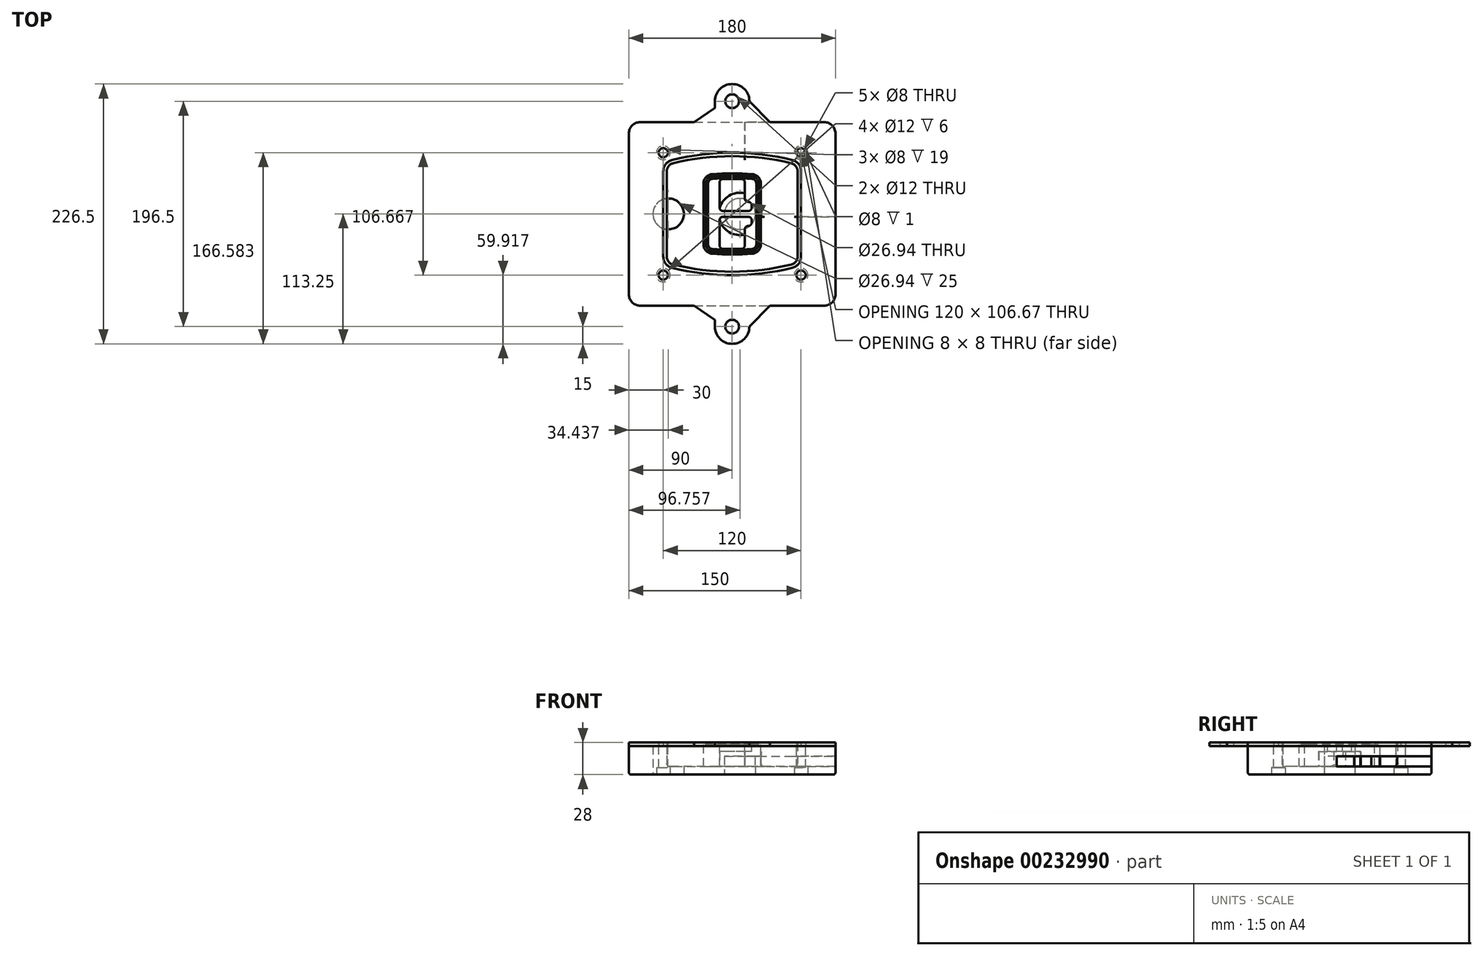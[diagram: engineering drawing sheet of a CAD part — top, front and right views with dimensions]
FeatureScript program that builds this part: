
annotation { "Feature Type Name" : "Feature", "Feature Type Description" : "" }
export const myFeature = defineFeature(function(context is Context, id is Id, definition is map)
    precondition{}
    {
        {
            var Q0;
            Q0=qCreatedBy(makeId("Top.planeOp"),FACE);
            var sketch = newSketch(context, id + "F0", { "sketchPlane" : qUnion([Q0])});
            skPoint(sketch, "E0.rect.middle", {"position": v(0, 0) * mm});
            skLineSegment(sketch, "E1.bottom", {"start": v(-80, -80) * mm, "end": v(80, -80) * mm});
            skLineSegment(sketch, "E1.top", {"start": v(-80, 80) * mm, "end": v(80, 80) * mm});
            skLineSegment(sketch, "E1.left", {"start": v(-90, -70) * mm, "end": v(-90, 70) * mm});
            skLineSegment(sketch, "E1.right", {"start": v(90, -70) * mm, "end": v(90, 70) * mm});
            skLineSegment(sketch, "E2", {"start": v(-90, 80) * mm, "end": v(90, -80) * mm, "construction": true});
            skLineSegment(sketch, "E3", {"start": v(90, 80) * mm, "end": v(-90, -80) * mm, "construction": true});
            skCircle(sketch, "E4", {"center": v(-60, 53.33) * mm, "radius": 4 * mm});
            skCircle(sketch, "E5", {"center": v(60, 53.33) * mm, "radius": 4 * mm});
            skCircle(sketch, "E6", {"center": v(60, -53.33) * mm, "radius": 4 * mm});
            skCircle(sketch, "E7", {"center": v(-60, -53.33) * mm, "radius": 4 * mm});
            skLineSegment(sketch, "E8", {"start": v(-60, 53.33) * mm, "end": v(60, 53.33) * mm, "construction": true});
            skLineSegment(sketch, "E9", {"start": v(60, 53.33) * mm, "end": v(60, -53.33) * mm, "construction": true});
            skLineSegment(sketch, "E10", {"start": v(60, -53.33) * mm, "end": v(-60, -53.33) * mm, "construction": true});
            skLineSegment(sketch, "E11", {"start": v(-60, -53.33) * mm, "end": v(-60, 53.33) * mm, "construction": true});
            skLineSegment(sketch, "E12", {"start": v(-60, 37.3) * mm, "end": v(-60, -37.3) * mm});
            skLineSegment(sketch, "E13", {"start": v(60, 37.3) * mm, "end": v(60, -37.3) * mm});
            skArc(sketch, "E14", {"start": v(52.38, 47.01) * mm, "mid": v(0, 53.33) * mm, "end": v(-52.38, 47.01) * mm});
            skArc(sketch, "E15", {"start": v(-52.38, -47.01) * mm, "mid": v(0, -53.33) * mm, "end": v(52.38, -47.01) * mm});
            skLineSegment(sketch, "E16", {"start": v(-60, 0) * mm, "end": v(60, 0) * mm, "construction": true});
            skPoint(sketch, "E17.visualSharp", {"position": v(-60, -45) * mm});
            skArc(sketch, "E17.filletArc", {"start": v(-60, -37.3) * mm, "mid": v(-57.87, -43.47) * mm, "end": v(-52.38, -47.01) * mm});
            skPoint(sketch, "E18.visualSharp", {"position": v(-60, 45) * mm});
            skArc(sketch, "E18.filletArc", {"start": v(-52.38, 47.01) * mm, "mid": v(-57.87, 43.47) * mm, "end": v(-60, 37.3) * mm});
            skPoint(sketch, "E19.visualSharp", {"position": v(60, 45) * mm});
            skArc(sketch, "E19.filletArc", {"start": v(60, 37.3) * mm, "mid": v(57.87, 43.47) * mm, "end": v(52.38, 47.01) * mm});
            skPoint(sketch, "E20.visualSharp", {"position": v(60, -45) * mm});
            skArc(sketch, "E20.filletArc", {"start": v(52.38, -47.01) * mm, "mid": v(57.87, -43.47) * mm, "end": v(60, -37.3) * mm});
            skPoint(sketch, "E21.visualSharp", {"position": v(-90, 80) * mm});
            skArc(sketch, "E21.filletArc", {"start": v(-80, 80) * mm, "mid": v(-87.07, 77.07) * mm, "end": v(-90, 70) * mm});
            skPoint(sketch, "E22.visualSharp", {"position": v(90, 80) * mm});
            skArc(sketch, "E22.filletArc", {"start": v(90, 70) * mm, "mid": v(87.07, 77.07) * mm, "end": v(80, 80) * mm});
            skPoint(sketch, "E23.visualSharp", {"position": v(90, -80) * mm});
            skArc(sketch, "E23.filletArc", {"start": v(80, -80) * mm, "mid": v(87.07, -77.07) * mm, "end": v(90, -70) * mm});
            skPoint(sketch, "E24.visualSharp", {"position": v(-90, -80) * mm});
            skArc(sketch, "E24.filletArc", {"start": v(-90, -70) * mm, "mid": v(-87.07, -77.07) * mm, "end": v(-80, -80) * mm});
            skArc(sketch, "E25.0", {"start": v(57, 37.3) * mm, "mid": v(55.5, 41.62) * mm, "end": v(51.67, 44.1) * mm});
            skLineSegment(sketch, "E25.1", {"start": v(57, 37.3) * mm, "end": v(57, -37.3) * mm});
            skArc(sketch, "E25.2", {"start": v(51.67, -44.1) * mm, "mid": v(55.5, -41.62) * mm, "end": v(57, -37.3) * mm});
            skArc(sketch, "E25.3", {"start": v(-51.67, -44.1) * mm, "mid": v(0, -50.33) * mm, "end": v(51.67, -44.1) * mm});
            skArc(sketch, "E25.4", {"start": v(-57, -37.3) * mm, "mid": v(-55.5, -41.62) * mm, "end": v(-51.67, -44.1) * mm});
            skArc(sketch, "E25.5", {"start": v(51.67, 44.1) * mm, "mid": v(0, 50.33) * mm, "end": v(-51.67, 44.1) * mm});
            skLineSegment(sketch, "E25.6", {"start": v(-57, 37.3) * mm, "end": v(-57, -37.3) * mm});
            skArc(sketch, "E25.7", {"start": v(-51.67, 44.1) * mm, "mid": v(-55.5, 41.62) * mm, "end": v(-57, 37.3) * mm});
            skArc(sketch, "E26.0", {"start": v(-53.33, 50.9) * mm, "mid": v(-61.01, 45.94) * mm, "end": v(-64, 37.3) * mm});
            skArc(sketch, "E26.1", {"start": v(53.33, 50.9) * mm, "mid": v(0, 57.33) * mm, "end": v(-53.33, 50.9) * mm});
            skArc(sketch, "E26.2", {"start": v(64, 37.3) * mm, "mid": v(61.01, 45.94) * mm, "end": v(53.33, 50.9) * mm});
            skLineSegment(sketch, "E26.3", {"start": v(64, 37.3) * mm, "end": v(64, -37.3) * mm});
            skArc(sketch, "E26.4", {"start": v(53.33, -50.9) * mm, "mid": v(61.01, -45.94) * mm, "end": v(64, -37.3) * mm});
            skLineSegment(sketch, "E26.5", {"start": v(-64, 37.3) * mm, "end": v(-64, -37.3) * mm});
            skArc(sketch, "E26.6", {"start": v(-53.33, -50.9) * mm, "mid": v(0, -57.33) * mm, "end": v(53.33, -50.9) * mm});
            skArc(sketch, "E26.7", {"start": v(-64, -37.3) * mm, "mid": v(-61.01, -45.94) * mm, "end": v(-53.33, -50.9) * mm});
            skSolve(sketch);
        }
        {
            var Q0;
            Q0=makeQuery(id+"F0.imprint","IMPRINT",FACE,{"disambiguationData":[TD([[makeQuery(id+"F0.imprint","IMPRINT",EDGE,{"derivedFrom":sQuery(id+"F0.wireOp",EDGE,"E1.bottom")}),1.0]])]});
            var Q1;
            Q1=makeQuery(id+"F0.imprint","IMPRINT",FACE,{"disambiguationData":[TD([[makeQuery(id+"F0.imprint","IMPRINT",EDGE,{"derivedFrom":sQuery(id+"F0.wireOp",EDGE,"E12")}),1.0]])]});
            var Q2;
            Q2=makeQuery(id+"F0.imprint","IMPRINT",FACE,{"disambiguationData":[TD([[makeQuery(id+"F0.imprint","IMPRINT",EDGE,{"derivedFrom":sQuery(id+"F0.wireOp",EDGE,"E25.0")}),1.0]])]});
            var Q3;
            Q3=makeQuery(id+"F0.imprint","IMPRINT",FACE,{"disambiguationData":[TD([[makeQuery(id+"F0.imprint","IMPRINT",EDGE,{"derivedFrom":sQuery(id+"F0.wireOp",EDGE,"E12")}),-1.0]])]});
            extrude(context, id + "F1", {"entities" : qUnion([Q0, Q1, Q2, Q3]), "oppositeDirection" : true, "depth" : 25 * mm});
        }
        {
            var Q0;
            Q0=makeQuery(id+"F0.imprint","IMPRINT",FACE,{"disambiguationData":[TD([[makeQuery(id+"F0.imprint","IMPRINT",EDGE,{"derivedFrom":sQuery(id+"F0.wireOp",EDGE,"E12")}),1.0]])]});
            extrude(context, id + "F2", {"entities" : qUnion([Q0]), "operationType" : NewBodyOperationType.ADD, "depth" : 3 * mm});
        }
        {
            var Q0;
            Q0=makeQuery(id+"F0.imprint","IMPRINT",FACE,{"disambiguationData":[TD([[makeQuery(id+"F0.imprint","IMPRINT",EDGE,{"derivedFrom":sQuery(id+"F0.wireOp",EDGE,"E25.0")}),1.0]])]});
            extrude(context, id + "F3", {"entities" : qUnion([Q0]), "operationType" : NewBodyOperationType.REMOVE, "oppositeDirection" : true, "depth" : 18 * mm});
        }
        {
            var Q0;
            Q0=makeQuery(id+"F2.opExtrude","CAP_FACE",FACE,{"disambiguationData":[OSD([sQuery(id+"F0.wireOp",EDGE,"E12"),sQuery(id+"F0.wireOp",EDGE,"E13"),sQuery(id+"F0.wireOp",EDGE,"E14"),sQuery(id+"F0.wireOp",EDGE,"E15"),sQuery(id+"F0.wireOp",EDGE,"E17.filletArc"),sQuery(id+"F0.wireOp",EDGE,"E18.filletArc"),sQuery(id+"F0.wireOp",EDGE,"E19.filletArc"),sQuery(id+"F0.wireOp",EDGE,"E20.filletArc"),sQuery(id+"F0.wireOp",EDGE,"E25.0"),sQuery(id+"F0.wireOp",EDGE,"E25.1"),sQuery(id+"F0.wireOp",EDGE,"E25.2"),sQuery(id+"F0.wireOp",EDGE,"E25.3"),sQuery(id+"F0.wireOp",EDGE,"E25.4"),sQuery(id+"F0.wireOp",EDGE,"E25.5"),sQuery(id+"F0.wireOp",EDGE,"E25.6"),sQuery(id+"F0.wireOp",EDGE,"E25.7")])],"isStart":false});
            var sketch = newSketch(context, id + "F4", { "sketchPlane" : qUnion([Q0])});
            skArc(sketch, "E27.0", {"start": v(-17.7, -34.56) * mm, "mid": v(0, -35.33) * mm, "end": v(17.7, -34.56) * mm});
            skArc(sketch, "E28.0", {"start": v(17.7, 34.56) * mm, "mid": v(0, 35.33) * mm, "end": v(-17.7, 34.56) * mm});
            skLineSegment(sketch, "E29", {"start": v(-25, 26.59) * mm, "end": v(-25, -26.59) * mm});
            skLineSegment(sketch, "E30", {"start": v(25, 26.59) * mm, "end": v(25, -26.59) * mm});
            skLineSegment(sketch, "E31", {"start": v(-25, 33.78) * mm, "end": v(25, 33.78) * mm, "construction": true});
            skLineSegment(sketch, "E32", {"start": v(-25, -33.78) * mm, "end": v(25, -33.78) * mm, "construction": true});
            skPoint(sketch, "E33.visualSharp", {"position": v(-25, 33.78) * mm});
            skArc(sketch, "E33.filletArc", {"start": v(-17.7, 34.56) * mm, "mid": v(-22.9, 32) * mm, "end": v(-25, 26.59) * mm});
            skPoint(sketch, "E34.visualSharp", {"position": v(25, 33.78) * mm});
            skArc(sketch, "E34.filletArc", {"start": v(25, 26.59) * mm, "mid": v(22.9, 32) * mm, "end": v(17.7, 34.56) * mm});
            skPoint(sketch, "E35.visualSharp", {"position": v(25, -33.78) * mm});
            skArc(sketch, "E35.filletArc", {"start": v(17.7, -34.56) * mm, "mid": v(22.9, -32) * mm, "end": v(25, -26.59) * mm});
            skPoint(sketch, "E36.visualSharp", {"position": v(-25, -33.78) * mm});
            skArc(sketch, "E36.filletArc", {"start": v(-25, -26.59) * mm, "mid": v(-22.9, -32) * mm, "end": v(-17.7, -34.56) * mm});
            skArc(sketch, "E37.0", {"start": v(51.67, 44.1) * mm, "mid": v(0, 50.33) * mm, "end": v(-51.67, 44.1) * mm});
            skArc(sketch, "E37.1", {"start": v(-51.67, 44.1) * mm, "mid": v(-55.5, 41.62) * mm, "end": v(-57, 37.3) * mm});
            skLineSegment(sketch, "E37.2", {"start": v(-57, 37.3) * mm, "end": v(-57, -37.3) * mm});
            skArc(sketch, "E37.3", {"start": v(-57, -37.3) * mm, "mid": v(-55.5, -41.62) * mm, "end": v(-51.67, -44.1) * mm});
            skArc(sketch, "E37.4", {"start": v(-51.67, -44.1) * mm, "mid": v(0, -50.33) * mm, "end": v(51.67, -44.1) * mm});
            skArc(sketch, "E37.5", {"start": v(51.67, -44.1) * mm, "mid": v(55.5, -41.62) * mm, "end": v(57, -37.3) * mm});
            skLineSegment(sketch, "E37.6", {"start": v(57, 37.3) * mm, "end": v(57, -37.3) * mm});
            skArc(sketch, "E37.7", {"start": v(57, 37.3) * mm, "mid": v(55.5, 41.62) * mm, "end": v(51.67, 44.1) * mm});
            skLineSegment(sketch, "E38.0", {"start": v(23, 26.59) * mm, "end": v(23, -26.59) * mm});
            skArc(sketch, "E38.1", {"start": v(17.53, -32.56) * mm, "mid": v(21.42, -30.64) * mm, "end": v(23, -26.59) * mm});
            skArc(sketch, "E38.2", {"start": v(-17.53, -32.56) * mm, "mid": v(0, -33.33) * mm, "end": v(17.53, -32.56) * mm});
            skArc(sketch, "E38.3", {"start": v(-23, -26.59) * mm, "mid": v(-21.42, -30.64) * mm, "end": v(-17.53, -32.56) * mm});
            skLineSegment(sketch, "E38.4", {"start": v(-23, 26.59) * mm, "end": v(-23, -26.59) * mm});
            skArc(sketch, "E38.5", {"start": v(23, 26.59) * mm, "mid": v(21.42, 30.64) * mm, "end": v(17.53, 32.56) * mm});
            skArc(sketch, "E38.6", {"start": v(-17.53, 32.56) * mm, "mid": v(-21.42, 30.64) * mm, "end": v(-23, 26.59) * mm});
            skArc(sketch, "E38.7", {"start": v(17.53, 32.56) * mm, "mid": v(0, 33.33) * mm, "end": v(-17.53, 32.56) * mm});
            skArc(sketch, "E39.0", {"start": v(21, 26.59) * mm, "mid": v(19.95, 29.29) * mm, "end": v(17.35, 30.57) * mm});
            skLineSegment(sketch, "E39.1", {"start": v(21, 26.59) * mm, "end": v(21, -26.59) * mm});
            skArc(sketch, "E39.2", {"start": v(17.35, -30.57) * mm, "mid": v(19.95, -29.29) * mm, "end": v(21, -26.59) * mm});
            skArc(sketch, "E39.3", {"start": v(-17.35, -30.57) * mm, "mid": v(0, -31.33) * mm, "end": v(17.35, -30.57) * mm});
            skArc(sketch, "E39.4", {"start": v(-21, -26.59) * mm, "mid": v(-19.95, -29.29) * mm, "end": v(-17.35, -30.57) * mm});
            skArc(sketch, "E39.5", {"start": v(17.35, 30.57) * mm, "mid": v(0, 31.33) * mm, "end": v(-17.35, 30.57) * mm});
            skLineSegment(sketch, "E39.6", {"start": v(-21, 26.59) * mm, "end": v(-21, -26.59) * mm});
            skArc(sketch, "E39.7", {"start": v(-17.35, 30.57) * mm, "mid": v(-19.95, 29.29) * mm, "end": v(-21, 26.59) * mm});
            skLineSegment(sketch, "E40", {"start": v(-25, 0) * mm, "end": v(25, 0) * mm, "construction": true});
            skLineSegment(sketch, "E41", {"start": v(-11, 5.5) * mm, "end": v(-11, 27.5) * mm});
            skLineSegment(sketch, "E42", {"start": v(-8, 30.5) * mm, "end": v(8, 30.5) * mm});
            skLineSegment(sketch, "E43", {"start": v(11, 27.5) * mm, "end": v(11, 13.5) * mm});
            skLineSegment(sketch, "E44", {"start": v(14, 10.5) * mm, "end": v(14, 10.5) * mm});
            skLineSegment(sketch, "E45", {"start": v(17, 7.5) * mm, "end": v(17, 5.5) * mm});
            skLineSegment(sketch, "E46", {"start": v(14, 2.5) * mm, "end": v(-8, 2.5) * mm});
            skPoint(sketch, "E47.visualSharp", {"position": v(-11, 30.5) * mm});
            skArc(sketch, "E47.filletArc", {"start": v(-8, 30.5) * mm, "mid": v(-10.12, 29.62) * mm, "end": v(-11, 27.5) * mm});
            skPoint(sketch, "E48.visualSharp", {"position": v(11, 30.5) * mm});
            skArc(sketch, "E48.filletArc", {"start": v(11, 27.5) * mm, "mid": v(10.12, 29.62) * mm, "end": v(8, 30.5) * mm});
            skPoint(sketch, "E49.visualSharp", {"position": v(11, 10.5) * mm});
            skArc(sketch, "E49.filletArc", {"start": v(11, 13.5) * mm, "mid": v(11.88, 11.38) * mm, "end": v(14, 10.5) * mm});
            skPoint(sketch, "E50.visualSharp", {"position": v(17, 10.5) * mm});
            skArc(sketch, "E50.filletArc", {"start": v(17, 7.5) * mm, "mid": v(16.12, 9.62) * mm, "end": v(14, 10.5) * mm});
            skPoint(sketch, "E51.visualSharp", {"position": v(17, 2.5) * mm});
            skArc(sketch, "E51.filletArc", {"start": v(14, 2.5) * mm, "mid": v(16.12, 3.38) * mm, "end": v(17, 5.5) * mm});
            skPoint(sketch, "E52.visualSharp", {"position": v(-11, 2.5) * mm});
            skArc(sketch, "E52.filletArc", {"start": v(-11, 5.5) * mm, "mid": v(-10.12, 3.38) * mm, "end": v(-8, 2.5) * mm});
            skLineSegment(sketch, "E53.0.MirrorCS", {"start": v(14, -2.5) * mm, "end": v(-8, -2.5) * mm});
            skArc(sketch, "E54.0.MirrorCS", {"start": v(-11, -5.5) * mm, "mid": v(-10.12, -3.38) * mm, "end": v(-8, -2.5) * mm});
            skLineSegment(sketch, "E55.0.MirrorCS", {"start": v(-11, -5.5) * mm, "end": v(-11, -27.5) * mm});
            skArc(sketch, "E56.0.MirrorCS", {"start": v(-8, -30.5) * mm, "mid": v(-10.12, -29.62) * mm, "end": v(-11, -27.5) * mm});
            skLineSegment(sketch, "E57.0.MirrorCS", {"start": v(-8, -30.5) * mm, "end": v(8, -30.5) * mm});
            skArc(sketch, "E58.0.MirrorCS", {"start": v(11, -27.5) * mm, "mid": v(10.12, -29.62) * mm, "end": v(8, -30.5) * mm});
            skLineSegment(sketch, "E59.0.MirrorCS", {"start": v(11, -27.5) * mm, "end": v(11, -13.5) * mm});
            skArc(sketch, "E60.0.MirrorCS", {"start": v(11, -13.5) * mm, "mid": v(11.88, -11.38) * mm, "end": v(14, -10.5) * mm});
            skArc(sketch, "E61.0.MirrorCS", {"start": v(17, -7.5) * mm, "mid": v(16.12, -9.62) * mm, "end": v(14, -10.5) * mm});
            skLineSegment(sketch, "E62.0.MirrorCS", {"start": v(17, -7.5) * mm, "end": v(17, -5.5) * mm});
            skArc(sketch, "E63.0.MirrorCS", {"start": v(14, -2.5) * mm, "mid": v(16.12, -3.38) * mm, "end": v(17, -5.5) * mm});
            skSolve(sketch);
        }
        {
            var Q0;
            Q0=makeQuery(id+"F4.imprint","IMPRINT",FACE,{"disambiguationData":[TD([[makeQuery(id+"F4.imprint","IMPRINT",EDGE,{"derivedFrom":sQuery(id+"F4.wireOp",EDGE,"E27.0")}),1.0]])]});
            var Q1;
            Q1=makeQuery(id+"F4.imprint","IMPRINT",FACE,{"disambiguationData":[TD([[makeQuery(id+"F4.imprint","IMPRINT",EDGE,{"derivedFrom":sQuery(id+"F4.wireOp",EDGE,"E38.0")}),-1.0]])]});
            var Q2;
            Q2=makeQuery(id+"F4.imprint","IMPRINT",FACE,{"disambiguationData":[TD([[makeQuery(id+"F4.imprint","IMPRINT",EDGE,{"derivedFrom":sQuery(id+"F4.wireOp",EDGE,"E39.0")}),1.0]])]});
            extrude(context, id + "F5", {"entities" : qUnion([Q0, Q1, Q2]), "operationType" : NewBodyOperationType.ADD, "endBound" : BoundingType.UP_TO_NEXT, "oppositeDirection" : true, "depth" : 25 * mm});
        }
        {
            var Q0;
            Q0=makeQuery(id+"F4.imprint","IMPRINT",FACE,{"disambiguationData":[TD([[makeQuery(id+"F4.imprint","IMPRINT",EDGE,{"derivedFrom":sQuery(id+"F4.wireOp",EDGE,"E38.0")}),-1.0]])]});
            extrude(context, id + "F6", {"entities" : qUnion([Q0]), "operationType" : NewBodyOperationType.REMOVE, "oppositeDirection" : true, "depth" : 2 * mm});
        }
        {
            var Q0;
            Q0=makeQuery(id+"F1.opExtrude","CAP_FACE",FACE,{"disambiguationData":[OSD([sQuery(id+"F0.wireOp",EDGE,"E1.bottom"),sQuery(id+"F0.wireOp",EDGE,"E1.top"),sQuery(id+"F0.wireOp",EDGE,"E1.left"),sQuery(id+"F0.wireOp",EDGE,"E1.right"),sQuery(id+"F0.wireOp",EDGE,"E4"),sQuery(id+"F0.wireOp",EDGE,"E5"),sQuery(id+"F0.wireOp",EDGE,"E6"),sQuery(id+"F0.wireOp",EDGE,"E7"),sQuery(id+"F0.wireOp",EDGE,"E21.filletArc"),sQuery(id+"F0.wireOp",EDGE,"E22.filletArc"),sQuery(id+"F0.wireOp",EDGE,"E23.filletArc"),sQuery(id+"F0.wireOp",EDGE,"E24.filletArc")])],"isStart":false});
            var sketch = newSketch(context, id + "F7", { "sketchPlane" : qUnion([Q0])});
            skCircle(sketch, "E64", {"center": v(6.76, 0) * mm, "radius": 13.47 * mm});
            skCircle(sketch, "E65", {"center": v(-55.56, 0) * mm, "radius": 13.47 * mm});
            skLineSegment(sketch, "E66", {"start": v(90, 0) * mm, "end": v(-90, 0) * mm});
            skCircle(sketch, "E67", {"center": v(6.76, 0) * mm, "radius": 18.47 * mm});
            skCircle(sketch, "E68", {"center": v(60, -53.33) * mm, "radius": 6 * mm});
            skCircle(sketch, "E69", {"center": v(-60, -53.33) * mm, "radius": 6 * mm});
            skCircle(sketch, "E70", {"center": v(-60, 53.33) * mm, "radius": 6 * mm});
            skCircle(sketch, "E71", {"center": v(60, 53.33) * mm, "radius": 6 * mm});
            skSolve(sketch);
        }
        {
            var Q0;
            {var subQ1=sQuery(id+"F7.wireOp",EDGE,"E66");var subQ4=sQuery(id+"F7.wireOp",EDGE,"E64");var subQ6=makeQuery(id+"F7.imprint","INTERSECT",VERTEX,{"disambiguationData":[OD(0.0)],"derivedFrom":[subQ4,subQ1]});Q0=makeQuery(id+"F7.imprint","IMPRINT",FACE,{"disambiguationData":[TD([[makeQuery(id+"F7.imprint","IMPRINT",EDGE,{"disambiguationData":[TD([[subQ6,-1.0]])],"derivedFrom":subQ4}),-1.0]])]});}
            var Q1;
            {var subQ0=sQuery(id+"F7.wireOp",EDGE,"E66");var subQ1=sQuery(id+"F7.wireOp",EDGE,"E64");var subQ3=makeQuery(id+"F7.imprint","INTERSECT",VERTEX,{"disambiguationData":[OD(0.0)],"derivedFrom":[subQ1,subQ0]});Q1=makeQuery(id+"F7.imprint","IMPRINT",FACE,{"disambiguationData":[TD([[makeQuery(id+"F7.imprint","IMPRINT",EDGE,{"disambiguationData":[TD([[subQ3,-1.0]])],"derivedFrom":subQ1}),1.0]])]});}
            var Q2;
            {var subQ0=sQuery(id+"F7.wireOp",EDGE,"E66");var subQ1=sQuery(id+"F7.wireOp",EDGE,"E64");var subQ3=makeQuery(id+"F7.imprint","INTERSECT",VERTEX,{"disambiguationData":[OD(0.0)],"derivedFrom":[subQ1,subQ0]});Q2=makeQuery(id+"F7.imprint","IMPRINT",FACE,{"disambiguationData":[TD([[makeQuery(id+"F7.imprint","IMPRINT",EDGE,{"disambiguationData":[TD([[subQ3,1.0]])],"derivedFrom":subQ1}),1.0]])]});}
            var Q3;
            {var subQ1=sQuery(id+"F7.wireOp",EDGE,"E66");var subQ4=sQuery(id+"F7.wireOp",EDGE,"E64");var subQ6=makeQuery(id+"F7.imprint","INTERSECT",VERTEX,{"disambiguationData":[OD(0.0)],"derivedFrom":[subQ4,subQ1]});Q3=makeQuery(id+"F7.imprint","IMPRINT",FACE,{"disambiguationData":[TD([[makeQuery(id+"F7.imprint","IMPRINT",EDGE,{"disambiguationData":[TD([[subQ6,1.0]])],"derivedFrom":subQ4}),-1.0]])]});}
            extrude(context, id + "F8", {"entities" : qUnion([Q0, Q1, Q2, Q3]), "operationType" : NewBodyOperationType.ADD, "oppositeDirection" : true, "depth" : 20 * mm});
        }
        {
            var Q0;
            {var subQ0=sQuery(id+"F7.wireOp",EDGE,"E66");var subQ1=sQuery(id+"F7.wireOp",EDGE,"E64");var subQ3=makeQuery(id+"F7.imprint","INTERSECT",VERTEX,{"disambiguationData":[OD(0.0)],"derivedFrom":[subQ1,subQ0]});Q0=makeQuery(id+"F7.imprint","IMPRINT",FACE,{"disambiguationData":[TD([[makeQuery(id+"F7.imprint","IMPRINT",EDGE,{"disambiguationData":[TD([[subQ3,-1.0]])],"derivedFrom":subQ1}),1.0]])]});}
            var Q1;
            {var subQ0=sQuery(id+"F7.wireOp",EDGE,"E66");var subQ1=sQuery(id+"F7.wireOp",EDGE,"E64");var subQ3=makeQuery(id+"F7.imprint","INTERSECT",VERTEX,{"disambiguationData":[OD(0.0)],"derivedFrom":[subQ1,subQ0]});Q1=makeQuery(id+"F7.imprint","IMPRINT",FACE,{"disambiguationData":[TD([[makeQuery(id+"F7.imprint","IMPRINT",EDGE,{"disambiguationData":[TD([[subQ3,1.0]])],"derivedFrom":subQ1}),1.0]])]});}
            extrude(context, id + "F9", {"entities" : qUnion([Q0, Q1]), "operationType" : NewBodyOperationType.REMOVE, "oppositeDirection" : true, "depth" : 16 * mm});
        }
        {
            var Q0;
            {var subQ0=sQuery(id+"F7.wireOp",EDGE,"E66");var subQ1=sQuery(id+"F7.wireOp",EDGE,"E65");var subQ3=makeQuery(id+"F7.imprint","INTERSECT",VERTEX,{"disambiguationData":[OD(0.0)],"derivedFrom":[subQ1,subQ0]});Q0=makeQuery(id+"F7.imprint","IMPRINT",FACE,{"disambiguationData":[TD([[makeQuery(id+"F7.imprint","IMPRINT",EDGE,{"disambiguationData":[TD([[subQ3,-1.0]])],"derivedFrom":subQ1}),1.0]])]});}
            var Q1;
            {var subQ0=sQuery(id+"F7.wireOp",EDGE,"E66");var subQ1=sQuery(id+"F7.wireOp",EDGE,"E65");var subQ3=makeQuery(id+"F7.imprint","INTERSECT",VERTEX,{"disambiguationData":[OD(0.0)],"derivedFrom":[subQ1,subQ0]});Q1=makeQuery(id+"F7.imprint","IMPRINT",FACE,{"disambiguationData":[TD([[makeQuery(id+"F7.imprint","IMPRINT",EDGE,{"disambiguationData":[TD([[subQ3,1.0]])],"derivedFrom":subQ1}),1.0]])]});}
            extrude(context, id + "F10", {"entities" : qUnion([Q0, Q1]), "operationType" : NewBodyOperationType.REMOVE, "oppositeDirection" : true, "depth" : 25 * mm});
        }
        {
            var Q0;
            Q0=makeQuery(id+"F7.imprint","IMPRINT",FACE,{"disambiguationData":[TD([[makeQuery(id+"F7.imprint","IMPRINT",EDGE,{"derivedFrom":sQuery(id+"F7.wireOp",EDGE,"E68")}),1.0]])]});
            var Q1;
            Q1=makeQuery(id+"F7.imprint","IMPRINT",FACE,{"disambiguationData":[TD([[makeQuery(id+"F7.imprint","IMPRINT",EDGE,{"derivedFrom":makeQuery(id+"F1.opExtrude","CAP_EDGE",EDGE,{"disambiguationData":[OSD([sQuery(id+"F0.wireOp",EDGE,"E5")])],"isStart":false})}),-1.0]])]});
            var Q2;
            Q2=makeQuery(id+"F7.imprint","IMPRINT",FACE,{"disambiguationData":[TD([[makeQuery(id+"F7.imprint","IMPRINT",EDGE,{"derivedFrom":sQuery(id+"F7.wireOp",EDGE,"E69")}),1.0]])]});
            var Q3;
            Q3=makeQuery(id+"F7.imprint","IMPRINT",FACE,{"disambiguationData":[TD([[makeQuery(id+"F7.imprint","IMPRINT",EDGE,{"derivedFrom":makeQuery(id+"F1.opExtrude","CAP_EDGE",EDGE,{"disambiguationData":[OSD([sQuery(id+"F0.wireOp",EDGE,"E4")])],"isStart":false})}),-1.0]])]});
            var Q4;
            Q4=makeQuery(id+"F7.imprint","IMPRINT",FACE,{"disambiguationData":[TD([[makeQuery(id+"F7.imprint","IMPRINT",EDGE,{"derivedFrom":sQuery(id+"F7.wireOp",EDGE,"E70")}),1.0]])]});
            var Q5;
            Q5=makeQuery(id+"F7.imprint","IMPRINT",FACE,{"disambiguationData":[TD([[makeQuery(id+"F7.imprint","IMPRINT",EDGE,{"derivedFrom":makeQuery(id+"F1.opExtrude","CAP_EDGE",EDGE,{"disambiguationData":[OSD([sQuery(id+"F0.wireOp",EDGE,"E7")])],"isStart":false})}),-1.0]])]});
            var Q6;
            Q6=makeQuery(id+"F7.imprint","IMPRINT",FACE,{"disambiguationData":[TD([[makeQuery(id+"F7.imprint","IMPRINT",EDGE,{"derivedFrom":sQuery(id+"F7.wireOp",EDGE,"E71")}),1.0]])]});
            var Q7;
            Q7=makeQuery(id+"F7.imprint","IMPRINT",FACE,{"disambiguationData":[TD([[makeQuery(id+"F7.imprint","IMPRINT",EDGE,{"derivedFrom":makeQuery(id+"F1.opExtrude","CAP_EDGE",EDGE,{"disambiguationData":[OSD([sQuery(id+"F0.wireOp",EDGE,"E6")])],"isStart":false})}),-1.0]])]});
            extrude(context, id + "F11", {"entities" : qUnion([Q0, Q1, Q2, Q3, Q4, Q5, Q6, Q7]), "operationType" : NewBodyOperationType.REMOVE, "oppositeDirection" : true, "depth" : 6 * mm});
        }
        {
            var Q0;
            Q0=makeQuery(id+"F9.boolean.opBoolean","COPY",FACE,{"derivedFrom":makeQuery(id+"F9.opExtrude","CAP_FACE",FACE,{"disambiguationData":[OSD([sQuery(id+"F7.wireOp",EDGE,"E64")])],"isStart":false})});
            var sketch = newSketch(context, id + "F12", { "sketchPlane" : qUnion([Q0])});
            skArc(sketch, "E72.0", {"start": v(11, -88.19) * mm, "mid": v(97.1, -83.6) * mm, "end": v(92.5, 2.5) * mm});
            skLineSegment(sketch, "E72.1", {"start": v(11, -17.97) * mm, "end": v(11, -17.97) * mm});
            skLineSegment(sketch, "E73", {"start": v(92.5, -105.13) * mm, "end": v(102.3, -105.13) * mm});
            skLineSegment(sketch, "E74.0", {"start": v(92.5, 2.5) * mm, "end": v(14, 2.5) * mm});
            skArc(sketch, "E74.1", {"start": v(14, 2.5) * mm, "mid": v(16.12, 3.38) * mm, "end": v(17, 5.5) * mm});
            skLineSegment(sketch, "E74.2", {"start": v(17, 7.5) * mm, "end": v(17, 5.5) * mm});
            skArc(sketch, "E74.3", {"start": v(17, 7.5) * mm, "mid": v(16.12, 9.62) * mm, "end": v(14, 10.5) * mm});
            skArc(sketch, "E74.4", {"start": v(11, 13.5) * mm, "mid": v(11.88, 11.38) * mm, "end": v(14, 10.5) * mm});
            skLineSegment(sketch, "E74.5", {"start": v(11, 13.5) * mm, "end": v(11, -88.19) * mm});
            skLineSegment(sketch, "E74.7", {"start": v(92.5, -2.5) * mm, "end": v(14, -2.5) * mm});
            skArc(sketch, "E74.8", {"start": v(14, -2.5) * mm, "mid": v(16.12, -3.38) * mm, "end": v(17, -5.5) * mm});
            skLineSegment(sketch, "E74.9", {"start": v(17, -7.5) * mm, "end": v(17, -5.5) * mm});
            skArc(sketch, "E74.10", {"start": v(17, -7.5) * mm, "mid": v(16.12, -9.62) * mm, "end": v(14, -10.5) * mm});
            skArc(sketch, "E74.11", {"start": v(11, -13.5) * mm, "mid": v(11.88, -11.38) * mm, "end": v(14, -10.5) * mm});
            skLineSegment(sketch, "E74.12", {"start": v(11, -17.97) * mm, "end": v(11, -13.5) * mm});
            skPoint(sketch, "E75.orphan", {"position": v(11, -27.5) * mm});
            skPoint(sketch, "E76.orphan", {"position": v(-8, -2.5) * mm});
            skPoint(sketch, "E77.orphan", {"position": v(-8, 2.5) * mm});
            skPoint(sketch, "E78.orphan", {"position": v(11, 27.5) * mm});
            skSolve(sketch);
        }
        {
            var Q0;
            {var subQ7=sQuery(id+"F12.wireOp",EDGE,"E72.0");var subQ14=sQuery(id+"F12.wireOp",EDGE,"E72.1");var subQ16=sQuery(id+"F12.wireOp",EDGE,"E74.1");var subQ18=sQuery(id+"F12.wireOp",EDGE,"E74.8");Q0=qUnion([makeQuery(id+"F12.imprint","IMPRINT",FACE,{"disambiguationData":[TD([[makeQuery(id+"F12.imprint","IMPRINT",EDGE,{"derivedFrom":subQ7}),1.0]])]}),makeQuery(id+"F12.imprint","IMPRINT",FACE,{"disambiguationData":[TD([[makeQuery(id+"F12.imprint","IMPRINT",EDGE,{"derivedFrom":subQ14}),1.0]])]}),makeQuery(id+"F12.imprint","IMPRINT",FACE,{"disambiguationData":[TD([[makeQuery(id+"F12.imprint","IMPRINT",EDGE,{"derivedFrom":subQ16}),1.0]])]}),makeQuery(id+"F12.imprint","IMPRINT",FACE,{"disambiguationData":[TD([[makeQuery(id+"F12.imprint","IMPRINT",EDGE,{"derivedFrom":subQ18}),-1.0]])]})]);}
            var Q1;
            Q1=makeQuery(id+"F5.boolean.opBoolean","SPLIT",FACE,{"disambiguationData":[TD([makeQuery(id+"F5.opExtrude","SWEPT_FACE",FACE,{"disambiguationData":[OSD([sQuery(id+"F4.wireOp",EDGE,"E41")])]})])],"derivedFrom":makeQuery(id+"F3.boolean.opBoolean","COPY",FACE,{"derivedFrom":makeQuery(id+"F3.opExtrude","CAP_FACE",FACE,{"disambiguationData":[OSD([sQuery(id+"F0.wireOp",EDGE,"E25.0"),sQuery(id+"F0.wireOp",EDGE,"E25.1"),sQuery(id+"F0.wireOp",EDGE,"E25.2"),sQuery(id+"F0.wireOp",EDGE,"E25.3"),sQuery(id+"F0.wireOp",EDGE,"E25.4"),sQuery(id+"F0.wireOp",EDGE,"E25.5"),sQuery(id+"F0.wireOp",EDGE,"E25.6"),sQuery(id+"F0.wireOp",EDGE,"E25.7")])],"isStart":false})})});
            extrude(context, id + "F13", {"entities" : qUnion([Q0]), "operationType" : NewBodyOperationType.REMOVE, "endBound" : BoundingType.UP_TO_SURFACE, "endBoundEntityFace" : qUnion([Q1]), "depth" : 25 * mm});
        }
        {
            var Q0;
            Q0=makeQuery(id+"F3.boolean.opBoolean","COPY",EDGE,{"derivedFrom":makeQuery(id+"F3.opExtrude","CAP_EDGE",EDGE,{"disambiguationData":[OSD([sQuery(id+"F0.wireOp",EDGE,"E25.6")])],"isStart":false})});
            var Q1;
            Q1=makeQuery(id+"F8.boolean.opBoolean","INTERSECT",EDGE,{"derivedFrom":[makeQuery(id+"F5.opExtrude","SWEPT_FACE",FACE,{"disambiguationData":[OSD([sQuery(id+"F4.wireOp",EDGE,"E30")])]}),makeQuery(id+"F8.opExtrude","CAP_FACE",FACE,{"disambiguationData":[OSD([sQuery(id+"F7.wireOp",EDGE,"E67")])],"isStart":false})]});
            var Q2;
            Q2=makeQuery(id+"F8.boolean.opBoolean","INTERSECT",EDGE,{"disambiguationData":[OD(1.0)],"derivedFrom":[makeQuery(id+"F5.opExtrude","SWEPT_FACE",FACE,{"disambiguationData":[OSD([sQuery(id+"F4.wireOp",EDGE,"E30")])]}),makeQuery(id+"F8.opExtrude","SWEPT_FACE",FACE,{"disambiguationData":[OSD([sQuery(id+"F7.wireOp",EDGE,"E67")])]})]});
            var Q3;
            {var subQ0=makeQuery(id+"F3.boolean.opBoolean","COPY",FACE,{"derivedFrom":makeQuery(id+"F3.opExtrude","CAP_FACE",FACE,{"disambiguationData":[OSD([sQuery(id+"F0.wireOp",EDGE,"E25.0"),sQuery(id+"F0.wireOp",EDGE,"E25.1"),sQuery(id+"F0.wireOp",EDGE,"E25.2"),sQuery(id+"F0.wireOp",EDGE,"E25.3"),sQuery(id+"F0.wireOp",EDGE,"E25.4"),sQuery(id+"F0.wireOp",EDGE,"E25.5"),sQuery(id+"F0.wireOp",EDGE,"E25.6"),sQuery(id+"F0.wireOp",EDGE,"E25.7")])],"isStart":false})});var subQ1=sQuery(id+"F4.wireOp",EDGE,"E30");Q3=makeQuery(id+"F8.boolean.opBoolean","SPLIT",EDGE,{"disambiguationData":[TD([makeQuery(id+"F5.opExtrude","SWEPT_FACE",FACE,{"disambiguationData":[OSD([sQuery(id+"F4.wireOp",EDGE,"E35.filletArc")])]})])],"derivedFrom":makeQuery(id+"F5.opExtrude","TWEAK_EDGE",EDGE,{"derivedFrom":[subQ0,makeQuery(id+"F4.imprint","IMPRINT",EDGE,{"derivedFrom":subQ1})]})});}
            var Q4;
            {var subQ0=sQuery(id+"F0.wireOp",EDGE,"E25.0");var subQ1=sQuery(id+"F0.wireOp",EDGE,"E25.1");var subQ2=sQuery(id+"F0.wireOp",EDGE,"E25.2");var subQ3=sQuery(id+"F0.wireOp",EDGE,"E25.3");var subQ4=sQuery(id+"F0.wireOp",EDGE,"E25.4");var subQ5=sQuery(id+"F0.wireOp",EDGE,"E25.5");var subQ6=sQuery(id+"F0.wireOp",EDGE,"E25.6");var subQ7=sQuery(id+"F0.wireOp",EDGE,"E25.7");Q4=makeQuery(id+"F8.boolean.opBoolean","INTERSECT",EDGE,{"derivedFrom":[makeQuery(id+"F5.boolean.opBoolean","SPLIT",FACE,{"disambiguationData":[TD([makeQuery(id+"F2.opExtrude","SWEPT_FACE",FACE,{"disambiguationData":[OSD([subQ0])]})])],"derivedFrom":makeQuery(id+"F3.boolean.opBoolean","COPY",FACE,{"derivedFrom":makeQuery(id+"F3.opExtrude","CAP_FACE",FACE,{"disambiguationData":[OSD([subQ0,subQ1,subQ2,subQ3,subQ4,subQ5,subQ6,subQ7])],"isStart":false})})}),makeQuery(id+"F8.opExtrude","SWEPT_FACE",FACE,{"disambiguationData":[OSD([sQuery(id+"F7.wireOp",EDGE,"E67")])]})]});}
            var Q5;
            Q5=makeQuery(id+"F8.boolean.opBoolean","INTERSECT",EDGE,{"disambiguationData":[OD(0.0)],"derivedFrom":[makeQuery(id+"F5.opExtrude","SWEPT_FACE",FACE,{"disambiguationData":[OSD([sQuery(id+"F4.wireOp",EDGE,"E30")])]}),makeQuery(id+"F8.opExtrude","SWEPT_FACE",FACE,{"disambiguationData":[OSD([sQuery(id+"F7.wireOp",EDGE,"E67")])]})]});
            fillet(context, id + "F14", {"entities" : qUnion([Q0, Q1, Q2, Q3, Q4, Q5]), "radius" : 3 * mm, "tangentPropagation" : true, "allowEdgeOverflow" : false});
        }
        {
            var Q0;
            Q0=makeQuery(id+"F1.opExtrude","CAP_EDGE",EDGE,{"disambiguationData":[OSD([sQuery(id+"F0.wireOp",EDGE,"E1.bottom")])],"isStart":false});
            fillet(context, id + "F15", {"entities" : qUnion([Q0]), "radius" : 2 * mm, "tangentPropagation" : true, "allowEdgeOverflow" : false});
        }
        {
            var Q0;
            {var subQ0=sQuery(id+"F0.wireOp",EDGE,"E22.filletArc");var subQ1=sQuery(id+"F0.wireOp",EDGE,"E7");var subQ2=sQuery(id+"F0.wireOp",EDGE,"E6");var subQ3=sQuery(id+"F0.wireOp",EDGE,"E5");var subQ4=sQuery(id+"F0.wireOp",EDGE,"E4");var subQ5=sQuery(id+"F0.wireOp",EDGE,"E1.bottom");var subQ6=sQuery(id+"F0.wireOp",EDGE,"E21.filletArc");var subQ7=sQuery(id+"F0.wireOp",EDGE,"E1.top");var subQ8=sQuery(id+"F0.wireOp",EDGE,"E1.left");var subQ9=sQuery(id+"F0.wireOp",EDGE,"E1.right");var subQ10=sQuery(id+"F0.wireOp",EDGE,"E23.filletArc");var subQ11=sQuery(id+"F0.wireOp",EDGE,"E24.filletArc");Q0=makeQuery(id+"F2.boolean.opBoolean","SPLIT",FACE,{"disambiguationData":[TD([makeQuery(id+"F1.opExtrude","SWEPT_FACE",FACE,{"disambiguationData":[OSD([subQ5])]})])],"derivedFrom":makeQuery(id+"F1.opExtrude","CAP_FACE",FACE,{"disambiguationData":[OSD([subQ5,subQ7,subQ8,subQ9,subQ4,subQ3,subQ2,subQ1,subQ6,subQ0,subQ10,subQ11])],"isStart":true})});}
            var sketch = newSketch(context, id + "F16", { "sketchPlane" : qUnion([Q0])});
            skArc(sketch, "E79.0", {"start": v(-80, 80) * mm, "mid": v(-87.07, 77.07) * mm, "end": v(-90, 70) * mm});
            skLineSegment(sketch, "E79.1", {"start": v(-90, -70) * mm, "end": v(-90, 70) * mm});
            skLineSegment(sketch, "E79.2", {"start": v(-80, 80) * mm, "end": v(80, 80) * mm});
            skArc(sketch, "E79.3", {"start": v(90, 70) * mm, "mid": v(87.07, 77.07) * mm, "end": v(80, 80) * mm});
            skLineSegment(sketch, "E79.4", {"start": v(90, -70) * mm, "end": v(90, 70) * mm});
            skArc(sketch, "E79.5", {"start": v(80, -80) * mm, "mid": v(87.07, -77.07) * mm, "end": v(90, -70) * mm});
            skLineSegment(sketch, "E79.6", {"start": v(-80, -80) * mm, "end": v(80, -80) * mm});
            skArc(sketch, "E79.7", {"start": v(-90, -70) * mm, "mid": v(-87.07, -77.07) * mm, "end": v(-80, -80) * mm});
            skCircle(sketch, "E79.8", {"center": v(-60, -53.33) * mm, "radius": 4 * mm});
            skCircle(sketch, "E79.9", {"center": v(-60, 53.33) * mm, "radius": 4 * mm});
            skCircle(sketch, "E79.10", {"center": v(60, 53.33) * mm, "radius": 4 * mm});
            skCircle(sketch, "E79.11", {"center": v(60, -53.33) * mm, "radius": 4 * mm});
            skArc(sketch, "E79.12", {"start": v(-52.38, -47.01) * mm, "mid": v(0, -53.33) * mm, "end": v(52.38, -47.01) * mm});
            skLineSegment(sketch, "E79.13", {"start": v(60, 37.3) * mm, "end": v(60, -37.3) * mm});
            skArc(sketch, "E79.14", {"start": v(52.38, -47.01) * mm, "mid": v(57.87, -43.47) * mm, "end": v(60, -37.3) * mm});
            skArc(sketch, "E79.15", {"start": v(52.38, 47.01) * mm, "mid": v(0, 53.33) * mm, "end": v(-52.38, 47.01) * mm});
            skArc(sketch, "E79.16", {"start": v(60, 37.3) * mm, "mid": v(57.87, 43.47) * mm, "end": v(52.38, 47.01) * mm});
            skLineSegment(sketch, "E79.17", {"start": v(-60, 37.3) * mm, "end": v(-60, -37.3) * mm});
            skArc(sketch, "E79.18", {"start": v(-52.38, 47.01) * mm, "mid": v(-57.87, 43.47) * mm, "end": v(-60, 37.3) * mm});
            skArc(sketch, "E79.19", {"start": v(-60, -37.3) * mm, "mid": v(-57.87, -43.47) * mm, "end": v(-52.38, -47.01) * mm});
            skLineSegment(sketch, "E80", {"start": v(0, 80) * mm, "end": v(0, 98.25) * mm});
            skLineSegment(sketch, "E81", {"start": v(-33, 80) * mm, "end": v(-15, 92.25) * mm});
            skLineSegment(sketch, "E82", {"start": v(-15, 92.25) * mm, "end": v(-15, 98.25) * mm});
            skLineSegment(sketch, "E83", {"start": v(33, 80) * mm, "end": v(15, 98) * mm});
            skLineSegment(sketch, "E84", {"start": v(15, 98) * mm, "end": v(15, 98.25) * mm});
            skCircle(sketch, "E85", {"center": v(0, 98.25) * mm, "radius": 6 * mm});
            skArc(sketch, "E86", {"start": v(15, 98.25) * mm, "mid": v(0, 113.25) * mm, "end": v(-15, 98.25) * mm});
            skLineSegment(sketch, "E87", {"start": v(-90, 0) * mm, "end": v(90, 0) * mm, "construction": true});
            skLineSegment(sketch, "E88.MirrorCS", {"start": v(-15, -92.25) * mm, "end": v(-15, -98.25) * mm});
            skLineSegment(sketch, "E89.MirrorCS", {"start": v(15, -98) * mm, "end": v(15, -98.25) * mm});
            skLineSegment(sketch, "E90.MirrorCS", {"start": v(-33, -80) * mm, "end": v(-15, -92.25) * mm});
            skLineSegment(sketch, "E91.MirrorCS", {"start": v(0, -80) * mm, "end": v(0, -98.25) * mm});
            skCircle(sketch, "E92.MirrorC", {"center": v(0, -98.25) * mm, "radius": 6 * mm});
            skLineSegment(sketch, "E93.MirrorCS", {"start": v(33, -80) * mm, "end": v(15, -98) * mm});
            skArc(sketch, "E94.MirrorCS", {"start": v(15, -98.25) * mm, "mid": v(0, -113.25) * mm, "end": v(-15, -98.25) * mm});
            skSolve(sketch);
        }
        {
            var Q0;
            Q0 = qSketchRegion(id + "F16", true);
            var Q1;
            Q1=makeQuery(id+"F2.opExtrude","CAP_FACE",FACE,{"disambiguationData":[OSD([sQuery(id+"F0.wireOp",EDGE,"E12"),sQuery(id+"F0.wireOp",EDGE,"E13"),sQuery(id+"F0.wireOp",EDGE,"E14"),sQuery(id+"F0.wireOp",EDGE,"E15"),sQuery(id+"F0.wireOp",EDGE,"E17.filletArc"),sQuery(id+"F0.wireOp",EDGE,"E18.filletArc"),sQuery(id+"F0.wireOp",EDGE,"E19.filletArc"),sQuery(id+"F0.wireOp",EDGE,"E20.filletArc"),sQuery(id+"F0.wireOp",EDGE,"E25.0"),sQuery(id+"F0.wireOp",EDGE,"E25.1"),sQuery(id+"F0.wireOp",EDGE,"E25.2"),sQuery(id+"F0.wireOp",EDGE,"E25.3"),sQuery(id+"F0.wireOp",EDGE,"E25.4"),sQuery(id+"F0.wireOp",EDGE,"E25.5"),sQuery(id+"F0.wireOp",EDGE,"E25.6"),sQuery(id+"F0.wireOp",EDGE,"E25.7")])],"isStart":false});
            extrude(context, id + "F17", {"entities" : qUnion([Q0]), "endBound" : BoundingType.UP_TO_SURFACE, "endBoundEntityFace" : qUnion([Q1]), "depth" : 25 * mm});
        }
    });
